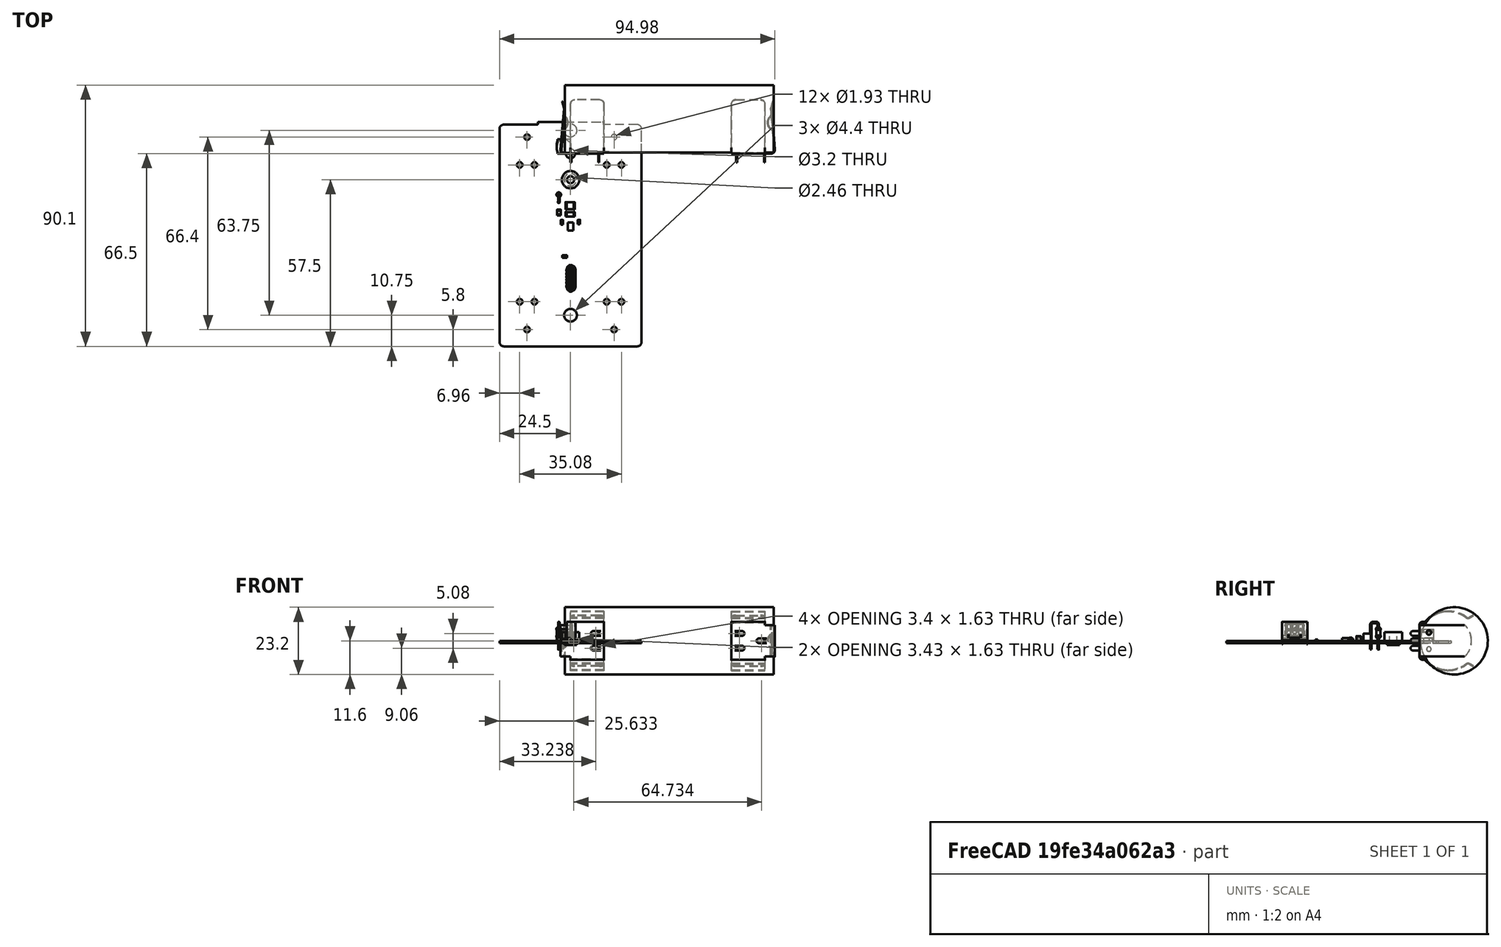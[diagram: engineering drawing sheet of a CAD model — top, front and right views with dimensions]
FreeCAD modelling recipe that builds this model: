
FCSTD DOCUMENT  (FreeCAD 0.20R24389 (Git))
Label: VX8BatteryPCB
License: All rights reserved
LicenseURL: http://en.wikipedia.org/wiki/All_rights_reserved
objects: Part::Feature×19, App::Link×14, App::Part×7, PartDesign::CoordinateSystem×2, Sketcher::SketchObject×1
note: 22 computed .brp shape members not serialized (recipe doc carries the construction recipe); baked Part::Feature solids carry a one-line shape summary decoded from their .brp

FEATURE [Part::Feature] Shape  label="TH1_R_Axial_DIN0204_L36mm_D16mm_P254mm_Vertical_99c942fc799d"
  Placement = pos=(-4.05,-14.18,0) rot=(0,0,-1;1.5708rad)
  shape: bbox 1.732 x 3.738 x 9.682 mm, 17 faces (baked)
FEATURE [Part::Feature] Shape001  label="R1_R_0603_1608Metric_e04d69ce8836"
  Placement = pos=(-2,-35.5,0) rot=(0,0,1;0rad)
  shape: bbox 1.6 x 0.8 x 0.45 mm, 26 faces (baked)
FEATURE [App::Link] R1_R_0603_1608Metric_e04d69ce8836_ln_  label="R9_R_0603_1608Metric_f0639e296eb6"
  LinkPlacement = pos=(2.3,-14.7,0) rot=(0,0,1;1.5708rad)
  LinkedObject = -> Shape001
  Placement = pos=(2.3,-14.7,0) rot=(0,0,1;1.5708rad)
FEATURE [Part::Feature] Shape002  label="U1_MP2672A_023df3fe17b2"
  Placement = pos=(0,-25.2,0) rot=(0,0,1;3.14159rad)
  shape: bbox 1.9 x 2.9 x 1 mm, 6 faces (baked)
FEATURE [App::Link] R1_R_0603_1608Metric_e04d69ce8836_ln_001  label="R10_R_0603_1608Metric_643c015a2d78"
  LinkPlacement = pos=(-0.15,-15.5,0) rot=(0,0,1;0rad)
  LinkedObject = -> Shape001
  Placement = pos=(-0.15,-15.5,0) rot=(0,0,1;0rad)
FEATURE [Part::Feature] Shape003  label="H1_Mounting_Wuerth_WA_SMSI_M3_H3mm_9774030360_f84d812b874e"
  Placement = pos=(0,-9,0) rot=(0,0,1;0rad)
  shape: bbox 6 x 6 x 4.4 mm, 6 faces (baked)
FEATURE [Part::Feature] Shape004  label="J1_MolexVerticalSMDUSBC_3ee5f35280ab"
  Placement = pos=(0.09,-43,2.7) rot=(0.57735,-0.57735,0.57735;4.18879rad)
  shape: bbox 3.14 x 8.74 x 7.7 mm, 785 faces (baked)
FEATURE [App::Link] R1_R_0603_1608Metric_e04d69ce8836_ln_002  label="R8_R_0603_1608Metric_a8c1d3861de0"
  LinkPlacement = pos=(3,-20.55,0) rot=(0,0,1;1.5708rad)
  LinkedObject = -> Shape001
  Placement = pos=(3,-20.55,0) rot=(0,0,1;1.5708rad)
FEATURE [App::Link] H1_Mounting_Wuerth_WA_SMSI_M3_H3mm_9774030360_f84d812b874e_ln_  label="H3_Mounting_Wuerth_WA_SMSI_M3_H3mm_9774030360_2b682b636820"
  LinkPlacement = pos=(0,8,0) rot=(0,0,1;0rad)
  LinkedObject = -> Shape003
  Placement = pos=(0,8,0) rot=(0,0,1;0rad)
FEATURE [Part::Feature] Shape005  label="C5_C_1210_3225Metric_d43db624757c"
  Placement = pos=(-0.15,-18,0) rot=(0,0,1;0rad)
  shape: bbox 3.2 x 2.5 x 2.5 mm, 28 faces (baked)
FEATURE [App::Link] R1_R_0603_1608Metric_e04d69ce8836_ln_003  label="R11_R_0603_1608Metric_aa7cc33fd4f6"
  LinkPlacement = pos=(-0.15,-13.95,0) rot=(0,0,1;3.14159rad)
  LinkedObject = -> Shape001
  Placement = pos=(-0.15,-13.95,0) rot=(0,0,1;3.14159rad)
FEATURE [Part::Feature] Shape006  label="C2_C_0603_1608Metric_7b14ea18a6a0"
  Placement = pos=(2.9,-23.65,0) rot=(0,0,1;1.5708rad)
  shape: bbox 0.8 x 1.6 x 0.8 mm, 28 faces (baked)
FEATURE [App::Link] R1_R_0603_1608Metric_e04d69ce8836_ln_004  label="R5_R_0603_1608Metric_4a0be65aeca5"
  LinkPlacement = pos=(-4.8,-26.8,0) rot=(0,0,-1;1.5708rad)
  LinkedObject = -> Shape001
  Placement = pos=(-4.8,-26.8,0) rot=(0,0,-1;1.5708rad)
FEATURE [Part::Feature] Shape007  label="C4_C_0805_2012Metric_7cbe0b741b72"
  Placement = pos=(-4,-20.3,0) rot=(0,0,1;1.5708rad)
  shape: bbox 1.25 x 2 x 1.25 mm, 28 faces (baked)
FEATURE [App::Link] R1_R_0603_1608Metric_e04d69ce8836_ln_005  label="R3_R_0603_1608Metric_3c15c3676faa"
  LinkPlacement = pos=(-4.75,-32.95,0) rot=(0,0,1;1.5708rad)
  LinkedObject = -> Shape001
  Placement = pos=(-4.75,-32.95,0) rot=(0,0,1;1.5708rad)
FEATURE [App::Link] R1_R_0603_1608Metric_e04d69ce8836_ln_006  label="R6_R_0603_1608Metric_2113a63b761c"
  LinkPlacement = pos=(-4.8,-23.7,0) rot=(0,0,1;1.5708rad)
  LinkedObject = -> Shape001
  Placement = pos=(-4.8,-23.7,0) rot=(0,0,1;1.5708rad)
FEATURE [App::Link] R1_R_0603_1608Metric_e04d69ce8836_ln_007  label="R2_R_0603_1608Metric_95794f961764"
  LinkPlacement = pos=(-2,-37,0) rot=(0,0,1;0rad)
  LinkedObject = -> Shape001
  Placement = pos=(-2,-37,0) rot=(0,0,1;0rad)
FEATURE [Part::Feature] Part__Feature  label="21700BatteryHolder-WithBattery"
  shape: bbox 14.99 x 21.69 x 20.57 mm, 136 faces (baked)
FEATURE [Part::Feature] Part__Feature001  label="21700BatteryHolder-WithBattery001"
  shape: bbox 14.99 x 21.69 x 20.57 mm, 136 faces (baked)
FEATURE [Part::Feature] Part__Feature002  label="21700BatteryHolder-WithBattery002"
  shape: bbox 72 x 23.2 x 23.2 mm, 3 faces (baked)
FEATURE [App::Part] _1700BatteryHolder_WithBattery  label="BT2_21700BatteryHolder-WithBattery003_6a512bc0f63d"
  Group = -> [Part__Feature,Part__Feature001,Part__Feature002]
  Origin = -> Origin008
  Placement = pos=(-15,-61.1,0) rot=(0.57735,0.57735,0.57735;2.0944rad)
FEATURE [Part::Feature] Shape008  label="D2_LED_0603_1608Metric_f960d8dfa779"
  Placement = pos=(-3,-23.7,0) rot=(0,0,-1;1.5708rad)
  shape: bbox 0.8 x 1.6 x 1.1 mm, 50 faces (baked)
FEATURE [App::Link] D2_LED_0603_1608Metric_f960d8dfa779_ln_  label="D1_LED_0603_1608Metric_8a45571821de"
  LinkPlacement = pos=(-3,-26.8,0) rot=(0,0,-1;1.5708rad)
  LinkedObject = -> Shape008
  Placement = pos=(-3,-26.8,0) rot=(0,0,-1;1.5708rad)
FEATURE [App::Link] C5_C_1210_3225Metric_d43db624757c_ln_  label="C1_C_1210_3225Metric_f1a0e6118902"
  LinkPlacement = pos=(2.5,-36.05,0) rot=(0,0,1;3.14159rad)
  LinkedObject = -> Shape005
  Placement = pos=(2.5,-36.05,0) rot=(0,0,1;3.14159rad)
FEATURE [App::Link] R1_R_0603_1608Metric_e04d69ce8836_ln_008  label="R7_R_0603_1608Metric_4a2389e36596"
  LinkPlacement = pos=(2.9,-26.95,0) rot=(0,0,1;1.5708rad)
  LinkedObject = -> Shape001
  Placement = pos=(2.9,-26.95,0) rot=(0,0,1;1.5708rad)
FEATURE [App::Link] H1_Mounting_Wuerth_WA_SMSI_M3_H3mm_9774030360_f84d812b874e_ln_001  label="H2_Mounting_Wuerth_WA_SMSI_M3_H3mm_9774030360_d314f7eeac2c"
  LinkPlacement = pos=(0,-55.75,0) rot=(0,0,1;0rad)
  LinkedObject = -> Shape003
  Placement = pos=(0,-55.75,0) rot=(0,0,1;0rad)
FEATURE [Part::Feature] Part__Feature003  label="21700BatteryHolder-NoBattery"
  shape: bbox 14.99 x 21.69 x 20.57 mm, 136 faces (baked)
FEATURE [Part::Feature] Part__Feature004  label="21700BatteryHolder-NoBattery001"
  shape: bbox 14.99 x 21.69 x 20.57 mm, 136 faces (baked)
FEATURE [App::Part] _1700BatteryHolder_NoBattery  label="BT1_21700BatteryHolder-NoBattery002_b1414afbb5f3"
  Group = -> [Part__Feature003,Part__Feature004]
  Origin = -> Origin009
  Placement = pos=(15,-61.1,0) rot=(0.57735,0.57735,0.57735;2.0944rad)
FEATURE [Part::Feature] Part__Feature005  label="inductor"
  shape: bbox 5 x 5 x 1 mm, 14 faces (baked)
FEATURE [Part::Feature] Part__Feature006  label="inductor001"
  shape: bbox 5 x 5 x 1 mm, 14 faces (baked)
FEATURE [Part::Feature] Part__Feature007  label="inductor002"
  shape: bbox 4.696 x 4.696 x 2 mm, 3 faces (baked)
FEATURE [App::Part] inductor  label="L1_inductor003_4a423316bf58"
  Group = -> [Part__Feature005,Part__Feature006,Part__Feature007]
  Origin = -> Origin010
  Placement = pos=(2.5,-29.2,0) rot=(0,0,1;1.5708rad)
FEATURE [App::Link] R1_R_0603_1608Metric_e04d69ce8836_ln_009  label="R4_R_0603_1608Metric_7f216eaa34ea"
  LinkPlacement = pos=(-4.75,-29.85,0) rot=(0,0,1;1.5708rad)
  LinkedObject = -> Shape001
  Placement = pos=(-4.75,-29.85,0) rot=(0,0,1;1.5708rad)
FEATURE [Part::Feature] Shape009  label="C3_C_1206_3216Metric_fab75bc0fda4"
  Placement = pos=(-0.15,-20.95,0) rot=(0,0,1;0rad)
  shape: bbox 3.2 x 1.6 x 1.6 mm, 28 faces (baked)
FEATURE [App::Part] Top_a240
  Group = -> [Shape,Shape001,R1_R_0603_1608Metric_e04d69ce8836_ln_,Shape002,R1_R_0603_1608Metric_e04d69ce8836_ln_001,Shape003,Shape004,R1_R_0603_1608Metric_e04d69ce8836_ln_002,H1_Mounting_Wuerth_WA_SMSI_M3_H3mm_9774030360_f84d812b874e_ln_,Shape005,R1_R_0603_1608Metric_e04d69ce8836_ln_003,Shape006,R1_R_0603_1608Metric_e04d69ce8836_ln_004,Shape007,R1_R_0603_1608Metric_e04d69ce8836_ln_005,+12 more]
  Origin = -> Origin003
FEATURE [App::Part] Step_Models_a240
  Group = -> [Top_a240]
  Origin = -> Origin002
FEATURE [PartDesign::CoordinateSystem] LCS_VX8Battery_1
  AttacherType = Attacher::AttachEngine3D
FEATURE [PartDesign::CoordinateSystem] Local_CS_a240
  AttacherType = Attacher::AttachEngine3D
FEATURE [Part::Feature] Pcb_a240
  Placement = pos=(-75,75,0) rot=(0,0,1;0rad)
  shape: bbox 49 x 77.45 x 0.8 mm, 48 faces (baked)
FEATURE [Sketcher::SketchObject] PCB_Sketch_a240
  FullyConstrained = false
  sketch-geometry (16):
    g0: LineSegment StartX=-23 StartY=-66.5 StartZ=0 EndX=23 EndY=-66.5 EndZ=0
    g1: LineSegment StartX=24.5 StartY=-65 StartZ=0 EndX=24.5 EndY=8.5 EndZ=0
    g2: LineSegment StartX=-24.5 StartY=8.5 StartZ=0 EndX=-24.5 EndY=-65 EndZ=0
    g3: LineSegment StartX=-23 StartY=10 StartZ=0 EndX=-11.5 EndY=10 EndZ=0
    g4: LineSegment StartX=23 StartY=10 StartZ=0 EndX=11.5 EndY=10 EndZ=0
    g5: LineSegment StartX=-11.241 StartY=10.259 StartZ=0 EndX=-11.241 EndY=10.688 EndZ=0
    g6: LineSegment StartX=-10.982 StartY=10.947 StartZ=0 EndX=10.982 EndY=10.947 EndZ=0
    g7: LineSegment StartX=11.241 StartY=10.688 StartZ=0 EndX=11.241 EndY=10.259 EndZ=0
    g8: ArcOfCircle CenterX=-23 CenterY=-65 CenterZ=0 NormalX=0 NormalY=0 NormalZ=1 AngleXU=0 Radius=1.5 StartAngle=3.14159 EndAngle=4.71239
    g9: ArcOfCircle CenterX=23 CenterY=-65 CenterZ=0 NormalX=0 NormalY=0 NormalZ=1 AngleXU=0 Radius=1.5 StartAngle=4.71239 EndAngle=6.28319
    g10: ArcOfCircle CenterX=-23 CenterY=8.5 CenterZ=0 NormalX=0 NormalY=0 NormalZ=1 AngleXU=0 Radius=1.5 StartAngle=1.5708 EndAngle=3.14159
    g11: ArcOfCircle CenterX=-11.5 CenterY=10.259 CenterZ=0 NormalX=0 NormalY=0 NormalZ=1 AngleXU=0 Radius=0.259 StartAngle=4.71239 EndAngle=6.28319
    g12: ArcOfCircle CenterX=-10.982 CenterY=10.688 CenterZ=0 NormalX=0 NormalY=0 NormalZ=1 AngleXU=0 Radius=0.259 StartAngle=1.5708 EndAngle=3.14159
    g13: ArcOfCircle CenterX=10.982 CenterY=10.688 CenterZ=0 NormalX=0 NormalY=0 NormalZ=1 AngleXU=0 Radius=0.259 StartAngle=0 EndAngle=1.5708
    g14: ArcOfCircle CenterX=11.5 CenterY=10.259 CenterZ=0 NormalX=0 NormalY=0 NormalZ=1 AngleXU=0 Radius=0.259 StartAngle=3.14159 EndAngle=4.71239
    g15: ArcOfCircle CenterX=23 CenterY=8.5 CenterZ=0 NormalX=0 NormalY=0 NormalZ=1 AngleXU=0 Radius=1.5 StartAngle=0 EndAngle=1.5708
  constraints (16):
    c: Coincident(g2,g8)
    c: Coincident(g2,g10)
    c: Coincident(g0,g8)
    c: Coincident(g3,g10)
    c: Coincident(g11,g3)
    c: Coincident(g11,g5)
    c: Coincident(g5,g12)
    c: Coincident(g12,g6)
    c: Coincident(g6,g13)
    c: Coincident(g7,g14)
    c: Coincident(g7,g13)
    c: Coincident(g4,g14)
    c: Coincident(g0,g9)
    c: Coincident(g4,g15)
    c: Coincident(g9,g1)
    c: Coincident(g1,g15)
FEATURE [App::Part] Board_Geoms_a240
  Group = -> [Local_CS_a240,Pcb_a240,PCB_Sketch_a240]
  Origin = -> Origin
FEATURE [App::Part] Board_a240  label="VX8Battery"
  Group = -> [Step_Models_a240,LCS_VX8Battery_1,Board_Geoms_a240]
  Origin = -> Origin001
